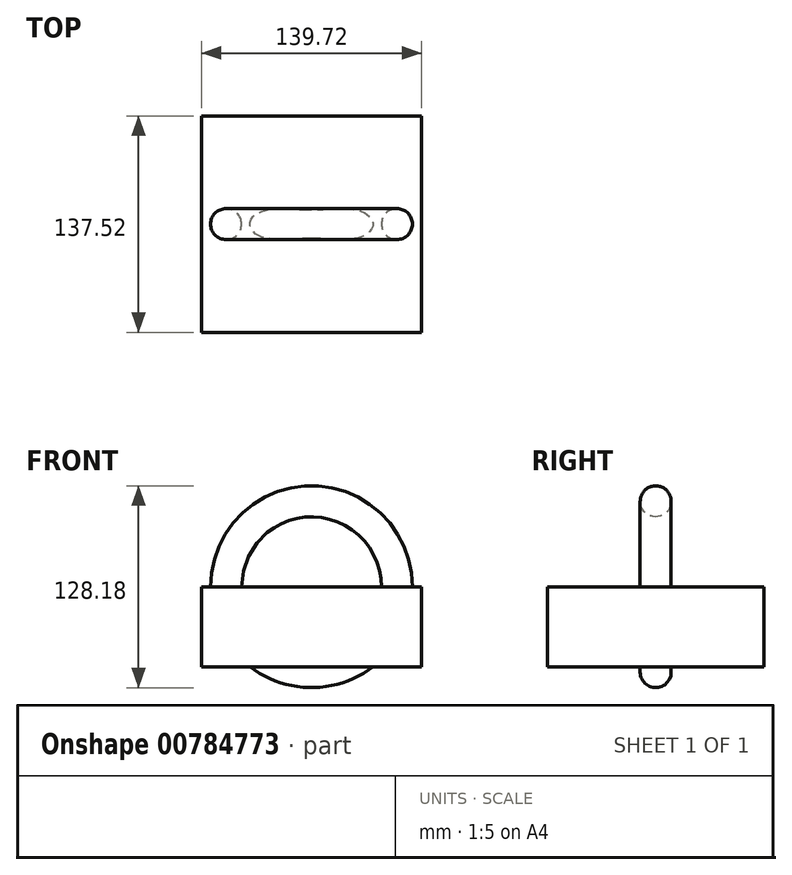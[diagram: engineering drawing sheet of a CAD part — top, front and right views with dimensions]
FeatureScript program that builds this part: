
annotation { "Feature Type Name" : "Feature", "Feature Type Description" : "" }
export const myFeature = defineFeature(function(context is Context, id is Id, definition is map)
    precondition{}
    {
        {
            var Q0;
            Q0=qCreatedBy(makeId("Top.planeOp"),FACE);
            var sketch = newSketch(context, id + "F0", { "sketchPlane" : qUnion([Q0])});
            skLineSegment(sketch, "E0.bottom", {"start": v(69.86, -68.76) * mm, "end": v(-69.86, -68.76) * mm});
            skLineSegment(sketch, "E0.top", {"start": v(69.86, 68.76) * mm, "end": v(-69.86, 68.76) * mm});
            skLineSegment(sketch, "E0.left", {"start": v(69.86, -68.76) * mm, "end": v(69.86, 68.76) * mm});
            skLineSegment(sketch, "E0.right", {"start": v(-69.86, -68.76) * mm, "end": v(-69.86, 68.76) * mm});
            skPoint(sketch, "E0.middle", {"position": v(0, 0) * mm});
            skLineSegment(sketch, "E1", {"start": v(0, 68.76) * mm, "end": v(0, -68.76) * mm});
            skSolve(sketch);
        }
        {
            var Q0;
            Q0=qCreatedBy(makeId("Top.planeOp"),FACE);
            var sketch = newSketch(context, id + "F1", { "sketchPlane" : qUnion([Q0])});
            skCircle(sketch, "E2", {"center": v(54.26, 0) * mm, "radius": 9.82 * mm});
            skSolve(sketch);
        }
        {
            var Q0;
            {var subQ0=sQuery(id+"F0.wireOp",EDGE,"E0.left");Q0=makeQuery(id+"F0.imprint","IMPRINT",FACE,{"disambiguationData":[TD([[makeQuery(id+"F0.imprint","IMPRINT",EDGE,{"derivedFrom":subQ0}),1.0]])]});}
            var Q1;
            {var subQ0=sQuery(id+"F0.wireOp",EDGE,"E0.right");Q1=makeQuery(id+"F0.imprint","IMPRINT",FACE,{"disambiguationData":[TD([[makeQuery(id+"F0.imprint","IMPRINT",EDGE,{"derivedFrom":subQ0}),-1.0]])]});}
            extrude(context, id + "F2", {"entities" : qUnion([Q0, Q1]), "oppositeDirection" : true, "depth" : 50.8 * mm, "offsetDistance" : 25.4 * mm});
        }
        {
            var Q0;
            Q0=makeQuery(id+"F1.imprint","IMPRINT",FACE,{"disambiguationData":[TD([[makeQuery(id+"F1.imprint","IMPRINT",EDGE,{"derivedFrom":sQuery(id+"F1.wireOp",EDGE,"E2")}),1.0]])]});
            var Q1;
            Q1=sQuery(id+"F0.wireOp",EDGE,"E1");
            revolve(context, id + "F3", {"operationType" : NewBodyOperationType.ADD, "surfaceOperationType" : NewSurfaceOperationType.NEW, "entities" : qUnion([Q0]), "axis" : qUnion([Q1]), "revolveType" : RevolveType.FULL});
        }
    });
